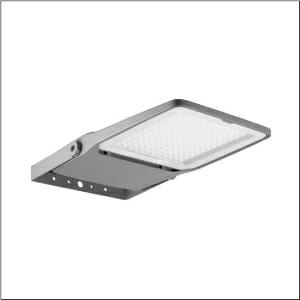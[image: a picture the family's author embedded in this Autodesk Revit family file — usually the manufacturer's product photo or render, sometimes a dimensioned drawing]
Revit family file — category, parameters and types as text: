
# Revit family: floodlight_fl_20_midi___rs17_5xa7682d1b2ac_3c54
name_source: partatom
category: Lighting Fixtures
units: mm (PartAtom-declared; Revit-internal decimal feet)

## family parameters
Cut with Voids When Loaded = No
Host = Face
Light Source = No
Part Type = Normal
Room Calculation Point = No
Round Connector Dimension = Use Diameter
Shared = No

## types (1)
- --- (1 x LED 3000K / CRI = 80 (unbekannt), 15350 lm, 3000K)
    Apparent Load = 142 VA
    CIE Flux Codes = 79 92 99 100 100
    Color Rendering = 80
    Color Temperature = 3000K
    Default Elevation = 1800 mm
    Description = Floodlight FL 20 midi, floodlight, primary light control with lens, of plastic, primary optical cover: protective disc, of toughened safety glass, transparent, light distribution: RS17, light emission: direct distribution, primary light characteristic: rotationally symmetric, installation type: surface-mounted, LED, High Power LED, rated luminous flux: 15.350lm, luminous efficacy: 108lm/W, light colour: 830, colour temperature: 3000K, control gear: ECG Plus, control: flexible luminous flux parameterisation, time-dependent luminous flux control, digital communication interface, power reduction, overheat protection, electronic power reduction, with terminal, 5-pole, max. 2.5mm², mains connection: 220..240V, AC, 50/60Hz, rated input power: 142W, LED unit, of diecast aluminium, powder-coated, Siteco® metallic grey (DB 702S), corrosivity category C5 mid according to DIN EN ISO 12944, incl. 1x M20 cable gland for cable Ø 6.5..12mm, length: 731mm, width: 450mm, height: 76mm, housing frame, of diecast aluminium, powder-coated, Siteco® metallic grey (DB 702S), wall fastening, of steel, powder-coated, Siteco® metallic grey (DB 702S), DALI, protection rating (complete): IP66, insulation class (complete): insulation class II (safety insulation), certification: CE, ENEC, VDE, protection symbol: D, permissible operating ambient temperature: -25..+40°C, permissible operating ambient temperature for outdoor applications: -40..+50°C, standard: DIN EN 12944, packaging unit: 1 piece

Light Distribution: RS17
    Height = 76 mm
    Lamp = 1 x LED 3000K / CRI >= 80 (unbekannt)
    Lamp Light Flux = 15350 lm
    Lamp count = 1
    Length = 731 mm
    Luminous efficacy = 108 lm/W
    Manufacturer = Siteco
    ModVariant = No
    Model = 5XA7682D1B2AC
    Mounting Place = Wall
    Mounting Type = Surface mounted
    Number of Poles = 1
    OnlyDefault = Yes
    Power Factor = 1
    Product Name = Floodlight FL 20 midi | RS17
    Product group = floodlight | wall mounted
    ProductGroupID = 2001
    Protection Class = Protection class II
    Protection Degree = IP 66
    RLX_Detail_Level = 1
    RLX_Emergency_Light_Flux = 0 lm
    RLX_Emergency_Type = 0
    RLX_Emergency_Type_DB = No
    RlxData = <blob elided: 86629 chars, md5=edee6ef2>
    Socket = socket
    Standby Power = 0 W
    System Light Flux = 15350 lm
    System Power = 142 W
    Type Comments = factory setting: luminous flux: 100 % | dim-lin: 254 | 489 mA
    Type Image = l_1005944.jpg
    URL = http://relux.com
    VarID = @adj_146701
    Voltage = 0 V
    Weight = 0.00 kg
    Width = 450 mm

## geometry (parser evidence)
native form markers: Blend x4, Sweep x13
no freeform markers — native parametric forms only
